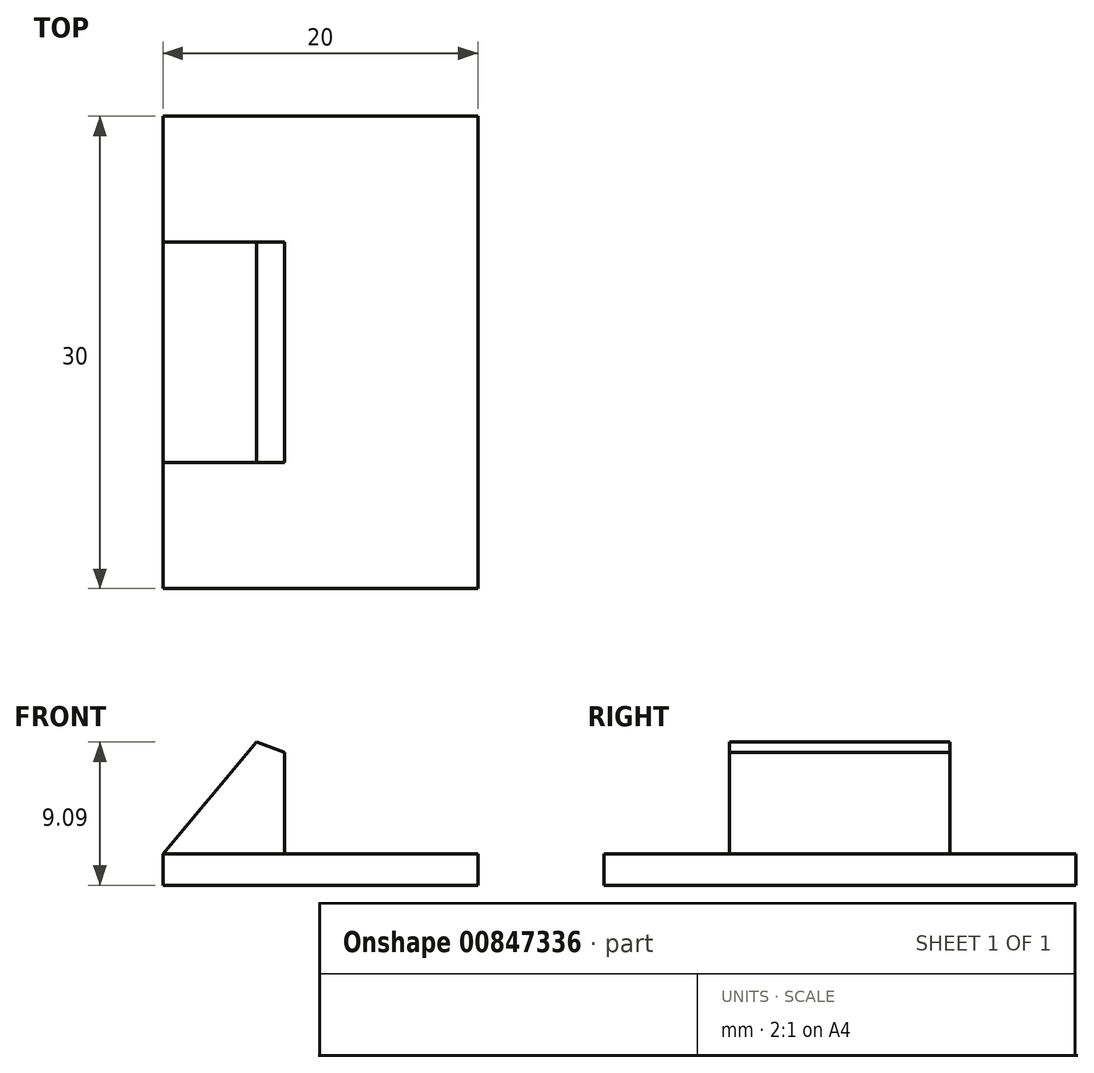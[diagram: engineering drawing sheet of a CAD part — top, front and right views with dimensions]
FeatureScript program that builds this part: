
annotation { "Feature Type Name" : "Feature", "Feature Type Description" : "" }
export const myFeature = defineFeature(function(context is Context, id is Id, definition is map)
    precondition{}
    {
        {
            var Q0;
            Q0=qCreatedBy(makeId("Top.planeOp"),FACE);
            var sketch = newSketch(context, id + "F0", { "sketchPlane" : qUnion([Q0])});
            skLineSegment(sketch, "E0.bottom", {"start": v(0, 0) * mm, "end": v(20, 0) * mm});
            skLineSegment(sketch, "E0.top", {"start": v(0, 30) * mm, "end": v(20, 30) * mm});
            skLineSegment(sketch, "E0.left", {"start": v(0, 0) * mm, "end": v(0, 30) * mm});
            skLineSegment(sketch, "E0.right", {"start": v(20, 0) * mm, "end": v(20, 30) * mm});
            skSolve(sketch);
        }
        {
            var Q0;
            Q0 = qSketchRegion(id + "F0", true);
            extrude(context, id + "F1", {"entities" : qUnion([Q0]), "depth" : 2 * mm, "offsetDistance" : 25 * mm});
        }
        {
            var Q0;
            Q0=makeQuery(id+"F1.opExtrude","SWEPT_FACE",FACE,{"disambiguationData":[OSD([sQuery(id+"F0.wireOp",EDGE,"E0.bottom")])]});
            var sketch = newSketch(context, id + "F2", { "sketchPlane" : qUnion([Q0])});
            skLineSegment(sketch, "E1", {"start": v(0, 2) * mm, "end": v(7.71, 11.2) * mm});
            skLineSegment(sketch, "E2", {"start": v(7.71, 11.2) * mm, "end": v(7.71, 2) * mm});
            skLineSegment(sketch, "E3", {"start": v(0, 2) * mm, "end": v(7.71, 2) * mm});
            skSolve(sketch);
        }
        {
            var Q0;
            Q0=makeQuery(id+"F2.imprint","IMPRINT",FACE,{"disambiguationData":[TD([[makeQuery(id+"F2.imprint","IMPRINT",EDGE,{"derivedFrom":sQuery(id+"F2.wireOp",EDGE,"E1")}),-1.0]])]});
            extrude(context, id + "F3", {"entities" : qUnion([Q0]), "operationType" : NewBodyOperationType.ADD, "oppositeDirection" : true, "depth" : 22 * mm, "offsetDistance" : 25 * mm, "hasSecondDirection" : true, "secondDirectionOppositeDirection" : true, "secondDirectionDepth" : 8 * mm});
        }
        {
            var Q0;
            Q0=makeQuery(id+"F3.opExtrude","SWEPT_EDGE",EDGE,{"disambiguationData":[OSD([sQuery(id+"F2.wireOp",EDGE,"E1"),sQuery(id+"F2.wireOp",EDGE,"E2")])]});
            chamfer(context, id + "F4", {"entities" : qUnion([Q0]), "width" : 1 * mm, "tangentPropagation" : true});
        }
    });
